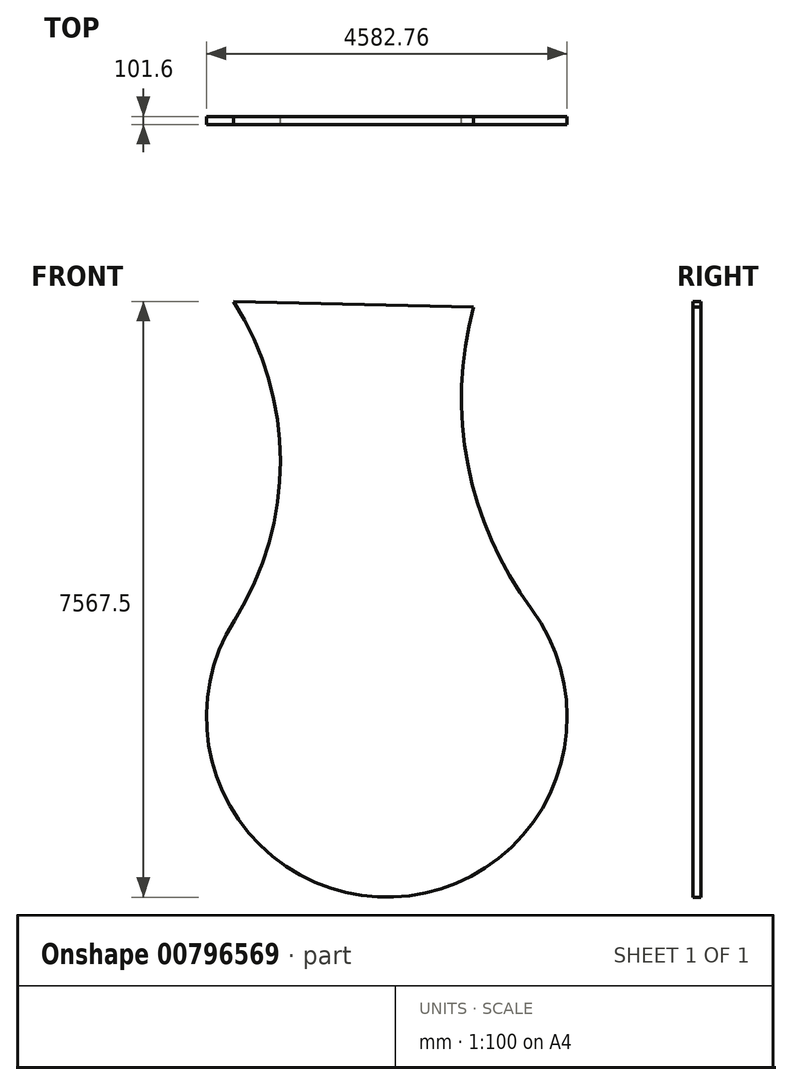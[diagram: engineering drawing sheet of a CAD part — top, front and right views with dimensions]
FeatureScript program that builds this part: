
annotation { "Feature Type Name" : "Feature", "Feature Type Description" : "" }
export const myFeature = defineFeature(function(context is Context, id is Id, definition is map)
    precondition{}
    {
        {
            var Q0;
            Q0=qCreatedBy(makeId("Front.planeOp"),FACE);
            var sketch = newSketch(context, id + "F0", { "sketchPlane" : qUnion([Q0])});
            skArc(sketch, "E0", {"start": v(8.8, 3540.7) * mm, "mid": v(2031.14, 25.18) * mm, "end": v(3782.86, 3683.08) * mm});
            skArc(sketch, "E1", {"start": v(3047.23, 7522.68) * mm, "mid": v(2975.08, 5518.59) * mm, "end": v(3782.86, 3683.08) * mm});
            skPoint(sketch, "E1.first.point", {"position": v(3782.86, 3683.08) * mm});
            skPoint(sketch, "E1.second.point", {"position": v(2898.46, 6184.56) * mm});
            skPoint(sketch, "E1.third.point", {"position": v(3047.23, 7522.68) * mm});
            skArc(sketch, "E2", {"start": v(8.8, 3540.7) * mm, "mid": v(594.02, 5567.16) * mm, "end": v(0, 7591.05) * mm});
            skPoint(sketch, "E2.first.point", {"position": v(8.8, 3540.7) * mm});
            skPoint(sketch, "E2.second.point", {"position": v(155.26, 7324.82) * mm});
            skPoint(sketch, "E2.third.point", {"position": v(0, 7591.05) * mm});
            skLineSegment(sketch, "E3", {"start": v(0, 7591.05) * mm, "end": v(3047.23, 7522.68) * mm});
            skPoint(sketch, "E4", {"position": v(4230.76, 2471.9) * mm});
            skPoint(sketch, "E5", {"position": v(-341.24, 2157.96) * mm});
            skPoint(sketch, "E6", {"position": v(2031.14, 25.18) * mm});
            skSolve(sketch);
        }
        {
            var Q0;
            Q0=makeQuery(id+"F0.imprint","IMPRINT",FACE,{"disambiguationData":[TD([[makeQuery(id+"F0.imprint","IMPRINT",EDGE,{"derivedFrom":sQuery(id+"F0.wireOp",EDGE,"E0")}),1.0]])]});
            extrude(context, id + "F1", {"entities" : qUnion([Q0]), "depth" : 101.6 * mm, "offsetDistance" : 25.4 * mm});
        }
    });
